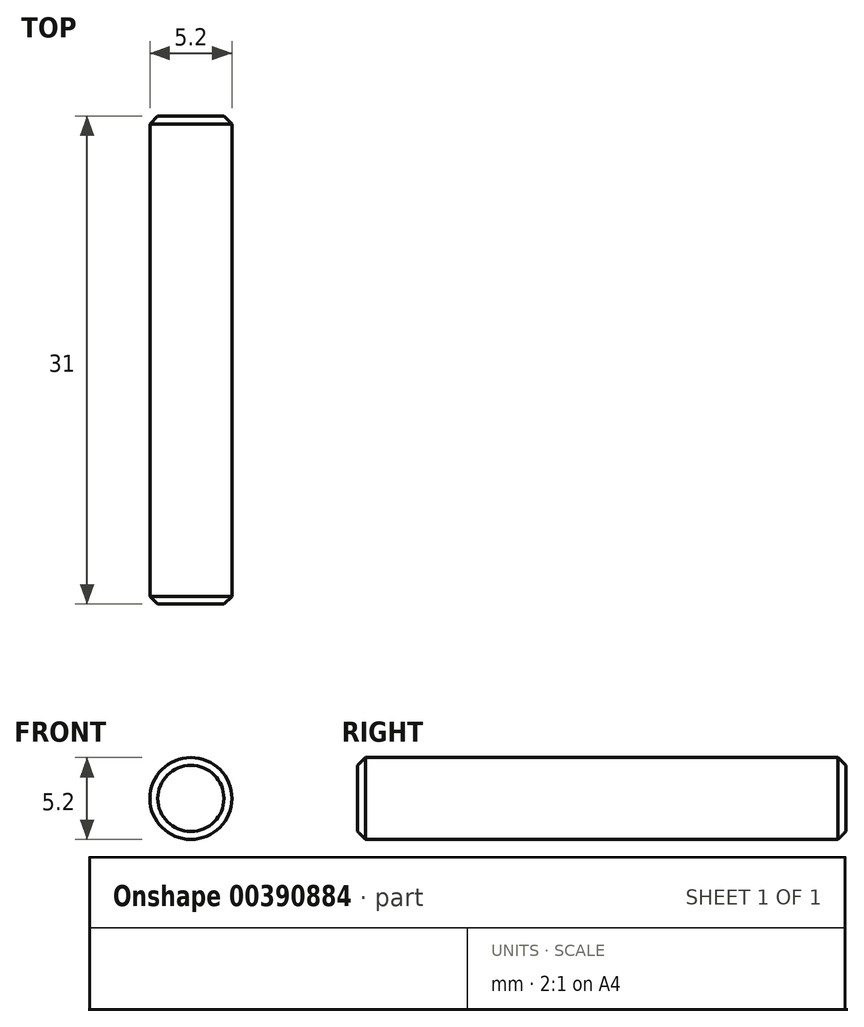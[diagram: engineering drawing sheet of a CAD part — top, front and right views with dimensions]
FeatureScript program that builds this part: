
annotation { "Feature Type Name" : "Feature", "Feature Type Description" : "" }
export const myFeature = defineFeature(function(context is Context, id is Id, definition is map)
    precondition{}
    {
        {
            var Q0;
            Q0=qCreatedBy(makeId("Front.planeOp"),FACE);
            var sketch = newSketch(context, id + "F0", { "sketchPlane" : qUnion([Q0])});
            skCircle(sketch, "E0", {"center": v(0, 0) * mm, "radius": 2.6 * mm});
            skSolve(sketch);
        }
        {
            var Q0;
            Q0 = qSketchRegion(id + "F0", true);
            extrude(context, id + "F1", {"entities" : qUnion([Q0]), "endBound" : BoundingType.SYMMETRIC, "depth" : 31 * mm});
        }
        {
            var Q0;
            Q0=makeQuery(id+"F1.opExtrude","CAP_EDGE",EDGE,{"disambiguationData":[OSD([sQuery(id+"F0.wireOp",EDGE,"E0")])],"isStart":false});
            var Q1;
            Q1=makeQuery(id+"F1.opExtrude","CAP_EDGE",EDGE,{"disambiguationData":[OSD([sQuery(id+"F0.wireOp",EDGE,"E0")])],"isStart":true});
            chamfer(context, id + "F2", {"entities" : qUnion([Q0, Q1]), "width" : .5 * mm, "tangentPropagation" : true});
        }
    });
